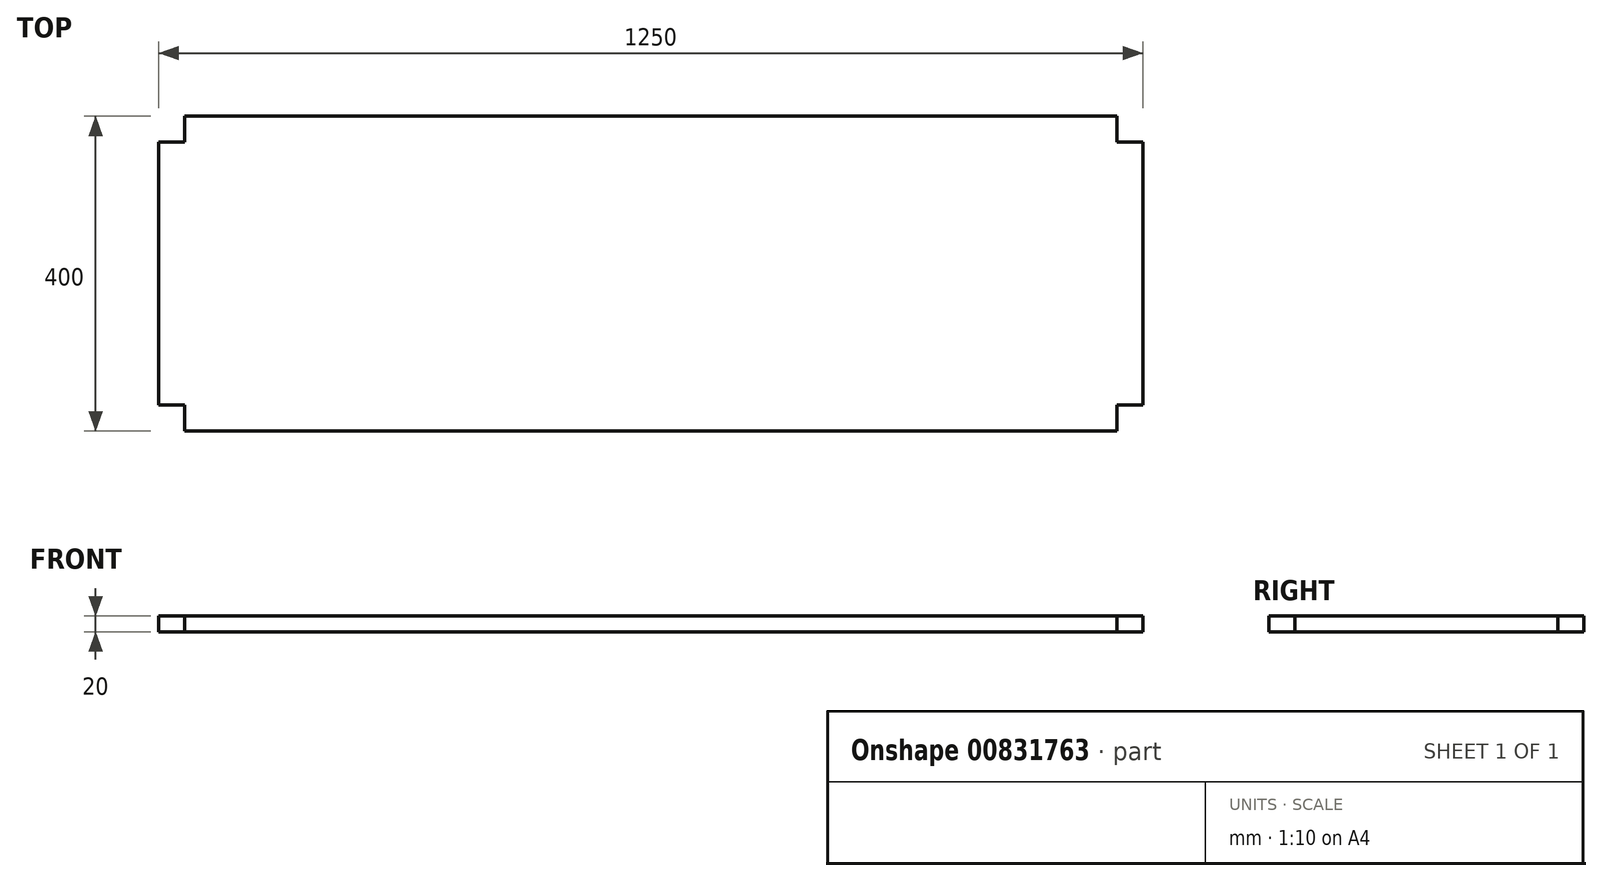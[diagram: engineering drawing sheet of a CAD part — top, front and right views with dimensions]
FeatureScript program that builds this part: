
annotation { "Feature Type Name" : "Feature", "Feature Type Description" : "" }
export const myFeature = defineFeature(function(context is Context, id is Id, definition is map)
    precondition{}
    {
        {
            var Q0;
            Q0=qCreatedBy(makeId("Top.planeOp"),FACE);
            var sketch = newSketch(context, id + "F0", { "sketchPlane" : qUnion([Q0])});
            skLineSegment(sketch, "E0.bottom", {"start": v(-247.02, 103.23) * mm, "end": v(936.98, 103.23) * mm});
            skLineSegment(sketch, "E0.top", {"start": v(-247.02, -296.77) * mm, "end": v(936.98, -296.77) * mm});
            skLineSegment(sketch, "E0.left", {"start": v(-280.02, 70.23) * mm, "end": v(-280.02, -263.77) * mm});
            skLineSegment(sketch, "E0.right", {"start": v(969.98, 70.23) * mm, "end": v(969.98, -263.77) * mm});
            skLineSegment(sketch, "E1.top", {"start": v(-280.02, 70.23) * mm, "end": v(-247.02, 70.23) * mm});
            skLineSegment(sketch, "E1.right", {"start": v(-247.02, 103.23) * mm, "end": v(-247.02, 70.23) * mm});
            skLineSegment(sketch, "E2.bottom", {"start": v(-280.02, -263.77) * mm, "end": v(-247.02, -263.77) * mm});
            skLineSegment(sketch, "E2.right", {"start": v(-247.02, -263.77) * mm, "end": v(-247.02, -296.77) * mm});
            skLineSegment(sketch, "E3.bottom", {"start": v(936.98, -263.77) * mm, "end": v(969.98, -263.77) * mm});
            skLineSegment(sketch, "E3.left", {"start": v(936.98, -263.77) * mm, "end": v(936.98, -296.77) * mm});
            skLineSegment(sketch, "E4.top", {"start": v(936.98, 70.23) * mm, "end": v(969.98, 70.23) * mm});
            skLineSegment(sketch, "E4.left", {"start": v(936.98, 103.23) * mm, "end": v(936.98, 70.23) * mm});
            skSolve(sketch);
        }
        {
            var Q0;
            Q0=makeQuery(id+"F0.imprint","IMPRINT",FACE,{"disambiguationData":[TD([[makeQuery(id+"F0.imprint","IMPRINT",EDGE,{"derivedFrom":sQuery(id+"F0.wireOp",EDGE,"E0.bottom")}),-1.0]])]});
            var sketch = newSketch(context, id + "F1", { "sketchPlane" : qUnion([Q0])});
            skSolve(sketch);
        }
        {
            var Q0;
            Q0=makeQuery(id+"F1.imprint","IMPRINT",FACE,{"disambiguationData":[TD([[makeQuery(id+"F1.imprint","IMPRINT",EDGE,{"derivedFrom":makeQuery(id+"F0.imprint","IMPRINT",EDGE,{"derivedFrom":sQuery(id+"F0.wireOp",EDGE,"E0.bottom")})}),-1.0]])]});
            var sketch = newSketch(context, id + "F2", { "sketchPlane" : qUnion([Q0])});
            skSolve(sketch);
        }
        {
            var Q0;
            Q0=makeQuery(id+"F2.imprint","IMPRINT",FACE,{"disambiguationData":[TD([[makeQuery(id+"F2.imprint","IMPRINT",EDGE,{"derivedFrom":makeQuery(id+"F1.imprint","IMPRINT",EDGE,{"derivedFrom":makeQuery(id+"F0.imprint","IMPRINT",EDGE,{"derivedFrom":sQuery(id+"F0.wireOp",EDGE,"E0.bottom")})})}),-1.0]])]});
            extrude(context, id + "F3", {"entities" : qUnion([Q0]), "depth" : 20 * mm, "offsetDistance" : 25 * mm});
        }
    });
